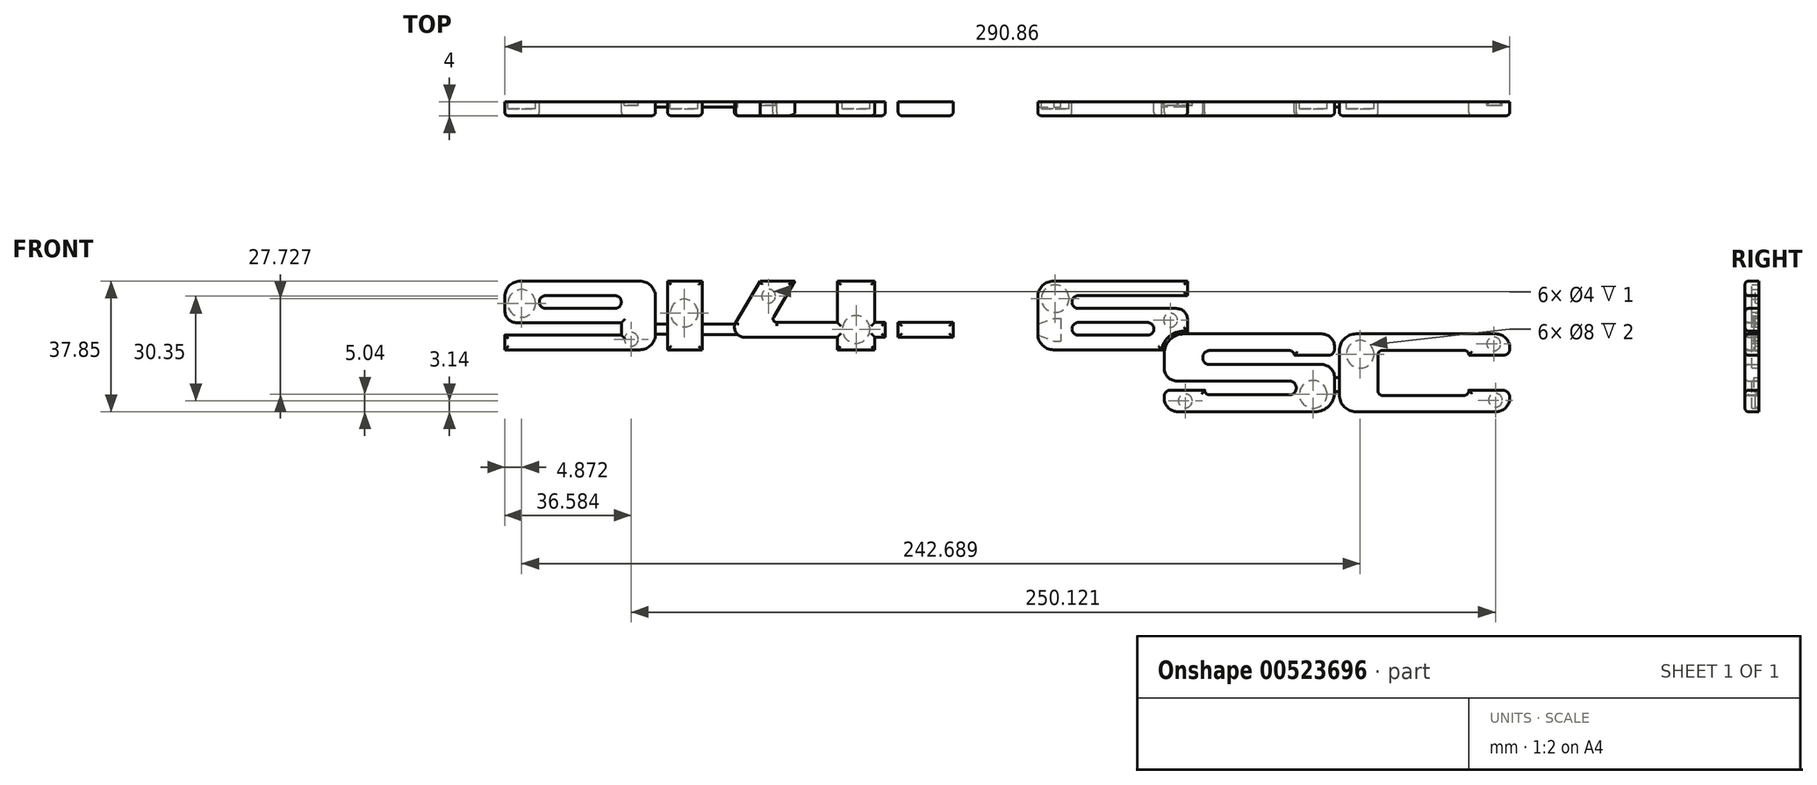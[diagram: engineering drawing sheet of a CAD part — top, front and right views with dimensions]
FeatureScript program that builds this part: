
annotation { "Feature Type Name" : "Feature", "Feature Type Description" : "" }
export const myFeature = defineFeature(function(context is Context, id is Id, definition is map)
    precondition{}
    {
        {
            var Q0;
            Q0=qCreatedBy(makeId("Front.planeOp"),FACE);
            var sketch = newSketch(context, id + "F0", { "sketchPlane" : qUnion([Q0])});
            skPoint(sketch, "E0", {"position": v(-109.13, 31.6) * mm});
            skPoint(sketch, "E1", {"position": v(-109.13, 11.72) * mm});
            skPoint(sketch, "E2", {"position": v(-65.54, 11.72) * mm});
            skPoint(sketch, "E3", {"position": v(-65.54, 31.6) * mm});
            skLineSegment(sketch, "E4.bottom", {"start": v(-104.63, 31.6) * mm, "end": v(-70.04, 31.6) * mm});
            skLineSegment(sketch, "E4.top", {"start": v(-109.13, 11.72) * mm, "end": v(-70.04, 11.72) * mm});
            skLineSegment(sketch, "E4.left", {"start": v(-109.13, 27.1) * mm, "end": v(-109.13, 23.04) * mm});
            skLineSegment(sketch, "E4.right", {"start": v(-65.54, 27.1) * mm, "end": v(-65.54, 16.22) * mm});
            skLineSegment(sketch, "E5.bottom", {"start": v(-109.13, 15.99) * mm, "end": v(-75.41, 15.99) * mm});
            skLineSegment(sketch, "E5.top", {"start": v(-105.62, 19.53) * mm, "end": v(-75.41, 19.53) * mm});
            skLineSegment(sketch, "E5.right", {"start": v(-75.41, 15.99) * mm, "end": v(-75.41, 19.53) * mm});
            skLineSegment(sketch, "E6.bottom", {"start": v(-77.15, 23.72) * mm, "end": v(-97.43, 23.72) * mm});
            skLineSegment(sketch, "E6.top", {"start": v(-77.15, 27.36) * mm, "end": v(-97.43, 27.36) * mm});
            skLineSegment(sketch, "E6.left", {"start": v(-75.41, 25.46) * mm, "end": v(-75.41, 25.62) * mm});
            skLineSegment(sketch, "E6.right", {"start": v(-99.16, 25.46) * mm, "end": v(-99.16, 25.62) * mm});
            skArc(sketch, "E7.filletArc", {"start": v(-104.63, 31.6) * mm, "mid": v(-107.81, 30.29) * mm, "end": v(-109.13, 27.1) * mm});
            skArc(sketch, "E8.filletArc", {"start": v(-65.54, 27.1) * mm, "mid": v(-66.86, 30.29) * mm, "end": v(-70.04, 31.6) * mm});
            skArc(sketch, "E9.filletArc", {"start": v(-70.04, 11.72) * mm, "mid": v(-66.86, 13.04) * mm, "end": v(-65.54, 16.22) * mm});
            skPoint(sketch, "E10.visualSharp", {"position": v(-99.16, 27.36) * mm});
            skArc(sketch, "E10.filletArc", {"start": v(-97.43, 27.36) * mm, "mid": v(-98.65, 26.85) * mm, "end": v(-99.16, 25.62) * mm});
            skPoint(sketch, "E11.visualSharp", {"position": v(-99.16, 23.72) * mm});
            skArc(sketch, "E11.filletArc", {"start": v(-99.16, 25.46) * mm, "mid": v(-98.65, 24.23) * mm, "end": v(-97.43, 23.72) * mm});
            skPoint(sketch, "E12.visualSharp", {"position": v(-75.41, 27.36) * mm});
            skArc(sketch, "E12.filletArc", {"start": v(-75.41, 25.62) * mm, "mid": v(-75.92, 26.85) * mm, "end": v(-77.15, 27.36) * mm});
            skPoint(sketch, "E13.visualSharp", {"position": v(-75.41, 23.72) * mm});
            skArc(sketch, "E13.filletArc", {"start": v(-77.15, 23.72) * mm, "mid": v(-75.92, 24.23) * mm, "end": v(-75.41, 25.46) * mm});
            skLineSegment(sketch, "E14.trimOffspring", {"start": v(-109.13, 15.99) * mm, "end": v(-109.13, 11.72) * mm});
            skPoint(sketch, "E15.visualSharp", {"position": v(-109.13, 19.53) * mm});
            skArc(sketch, "E15.filletArc", {"start": v(-109.13, 23.04) * mm, "mid": v(-108.1, 20.56) * mm, "end": v(-105.62, 19.53) * mm});
            skLineSegment(sketch, "E16", {"start": v(-62.04, 31.6) * mm, "end": v(-52.01, 31.6) * mm});
            skLineSegment(sketch, "E17", {"start": v(-62.04, 11.72) * mm, "end": v(-52.01, 11.72) * mm});
            skLineSegment(sketch, "E18.left", {"start": v(-62.04, 31.6) * mm, "end": v(-62.04, 11.72) * mm});
            skLineSegment(sketch, "E18.right", {"start": v(-52.01, 31.6) * mm, "end": v(-52.01, 11.72) * mm});
            skLineSegment(sketch, "E19", {"start": v(-31.25, 31.6) * mm, "end": v(-25.18, 31.6) * mm});
            skLineSegment(sketch, "E20.bottom", {"start": v(-12.94, 31.6) * mm, "end": v(-2.03, 31.6) * mm});
            skLineSegment(sketch, "E20.top", {"start": v(-12.94, 11.72) * mm, "end": v(-2.03, 11.72) * mm});
            skLineSegment(sketch, "E20.left", {"start": v(-12.94, 31.6) * mm, "end": v(-12.94, 19.68) * mm});
            skLineSegment(sketch, "E20.right", {"start": v(-2.03, 31.6) * mm, "end": v(-2.03, 19.68) * mm});
            skLineSegment(sketch, "E21.bottom", {"start": v(0.96, 19.68) * mm, "end": v(-2.03, 19.68) * mm});
            skLineSegment(sketch, "E21.top", {"start": v(0.96, 15.35) * mm, "end": v(-2.03, 15.35) * mm});
            skLineSegment(sketch, "E21.left", {"start": v(0.96, 19.68) * mm, "end": v(0.96, 15.35) * mm});
            skLineSegment(sketch, "E22", {"start": v(-35.26, 31.6) * mm, "end": v(-42.35, 19.59) * mm});
            skLineSegment(sketch, "E23", {"start": v(-25.18, 31.6) * mm, "end": v(-31.35, 21.25) * mm});
            skPoint(sketch, "E24", {"position": v(-30.43, 19.68) * mm});
            skLineSegment(sketch, "E25.trimOffspring", {"start": v(-12.94, 15.35) * mm, "end": v(-12.94, 11.72) * mm});
            skLineSegment(sketch, "E26.trimOffspring", {"start": v(-12.94, 15.35) * mm, "end": v(-39.77, 15.35) * mm});
            skLineSegment(sketch, "E27.trimOffspring", {"start": v(-2.03, 15.35) * mm, "end": v(-2.03, 11.72) * mm});
            skLineSegment(sketch, "E28.trimOffspring", {"start": v(-12.94, 19.68) * mm, "end": v(-30.43, 19.68) * mm});
            skLineSegment(sketch, "E29.trimOffspring", {"start": v(-35.26, 31.6) * mm, "end": v(-31.25, 31.6) * mm});
            skArc(sketch, "E30", {"start": v(-42.35, 19.59) * mm, "mid": v(-42.25, 16.75) * mm, "end": v(-39.77, 15.35) * mm});
            skArc(sketch, "E31", {"start": v(-31.35, 21.25) * mm, "mid": v(-31.35, 20.2) * mm, "end": v(-30.43, 19.68) * mm});
            skLineSegment(sketch, "E32", {"start": v(49.66, 31.6) * mm, "end": v(88.48, 31.6) * mm});
            skLineSegment(sketch, "E33", {"start": v(49.66, 11.72) * mm, "end": v(80.81, 11.72) * mm});
            skLineSegment(sketch, "E34.bottom", {"start": v(4.7, 19.69) * mm, "end": v(20.61, 19.69) * mm});
            skLineSegment(sketch, "E34.top", {"start": v(4.7, 15.35) * mm, "end": v(20.61, 15.35) * mm});
            skLineSegment(sketch, "E34.left", {"start": v(4.7, 19.69) * mm, "end": v(4.7, 15.35) * mm});
            skLineSegment(sketch, "E34.right", {"start": v(20.61, 19.69) * mm, "end": v(20.61, 15.35) * mm});
            skLineSegment(sketch, "E35", {"start": v(45.1, 26.4) * mm, "end": v(45.1, 16.28) * mm});
            skLineSegment(sketch, "E36", {"start": v(45.1, 26.4) * mm, "end": v(45.1, 27.06) * mm});
            skLineSegment(sketch, "E37", {"start": v(88.48, 31.6) * mm, "end": v(88.48, 27.39) * mm});
            skLineSegment(sketch, "E38.bottom", {"start": v(88.48, 27.39) * mm, "end": v(56.83, 27.39) * mm});
            skLineSegment(sketch, "E38.top", {"start": v(85.22, 23.67) * mm, "end": v(56.83, 23.67) * mm});
            skLineSegment(sketch, "E38.right", {"start": v(55, 25.56) * mm, "end": v(55, 25.5) * mm});
            skLineSegment(sketch, "E39.bottom", {"start": v(56.83, 19.61) * mm, "end": v(76.9, 19.61) * mm});
            skLineSegment(sketch, "E39.top", {"start": v(56.83, 15.93) * mm, "end": v(76.9, 15.93) * mm});
            skLineSegment(sketch, "E39.left", {"start": v(55, 17.78) * mm, "end": v(55, 17.76) * mm});
            skLineSegment(sketch, "E39.right", {"start": v(78.72, 17.78) * mm, "end": v(78.72, 17.76) * mm});
            skLineSegment(sketch, "E40.trimOffspring", {"start": v(88.48, 20.42) * mm, "end": v(88.48, 17.15) * mm});
            skPoint(sketch, "E41.visualSharp", {"position": v(45.1, 31.6) * mm});
            skArc(sketch, "E41.filletArc", {"start": v(49.66, 31.6) * mm, "mid": v(46.44, 30.27) * mm, "end": v(45.1, 27.06) * mm});
            skPoint(sketch, "E42.visualSharp", {"position": v(45.1, 11.72) * mm});
            skArc(sketch, "E42.filletArc", {"start": v(45.1, 16.28) * mm, "mid": v(46.44, 13.06) * mm, "end": v(49.66, 11.72) * mm});
            skPoint(sketch, "E43.visualSharp", {"position": v(88.48, 23.67) * mm});
            skArc(sketch, "E43.filletArc", {"start": v(88.48, 20.42) * mm, "mid": v(87.52, 22.72) * mm, "end": v(85.22, 23.67) * mm});
            skPoint(sketch, "E44.visualSharp", {"position": v(55, 27.39) * mm});
            skArc(sketch, "E44.filletArc", {"start": v(56.83, 27.39) * mm, "mid": v(55.54, 26.85) * mm, "end": v(55, 25.56) * mm});
            skPoint(sketch, "E45.visualSharp", {"position": v(55, 23.67) * mm});
            skArc(sketch, "E45.filletArc", {"start": v(55, 25.5) * mm, "mid": v(55.54, 24.21) * mm, "end": v(56.83, 23.67) * mm});
            skPoint(sketch, "E46.visualSharp", {"position": v(55, 19.61) * mm});
            skArc(sketch, "E46.filletArc", {"start": v(56.83, 19.61) * mm, "mid": v(55.54, 19.08) * mm, "end": v(55, 17.78) * mm});
            skPoint(sketch, "E47.visualSharp", {"position": v(55, 15.93) * mm});
            skArc(sketch, "E47.filletArc", {"start": v(55, 17.76) * mm, "mid": v(55.54, 16.47) * mm, "end": v(56.83, 15.93) * mm});
            skPoint(sketch, "E48.visualSharp", {"position": v(78.72, 19.61) * mm});
            skArc(sketch, "E48.filletArc", {"start": v(78.72, 17.78) * mm, "mid": v(78.19, 19.08) * mm, "end": v(76.9, 19.61) * mm});
            skPoint(sketch, "E49.visualSharp", {"position": v(78.72, 15.93) * mm});
            skArc(sketch, "E49.filletArc", {"start": v(76.9, 15.93) * mm, "mid": v(78.19, 16.47) * mm, "end": v(78.72, 17.76) * mm});
            skLineSegment(sketch, "E50", {"start": v(81.7, -1.92) * mm, "end": v(81.7, -1.8) * mm});
            skPoint(sketch, "E50.endSnap0", {"position": v(78.19, 16.47) * mm});
            skLineSegment(sketch, "E51", {"start": v(81.7, -1.92) * mm, "end": v(81.7, -2.2) * mm});
            skLineSegment(sketch, "E52", {"start": v(88.1, -6.24) * mm, "end": v(85.74, -6.24) * mm});
            skLineSegment(sketch, "E53", {"start": v(88.1, -6.24) * mm, "end": v(125.36, -6.24) * mm});
            skLineSegment(sketch, "E54", {"start": v(99.4, 16.3) * mm, "end": v(87.35, 16.3) * mm});
            skLineSegment(sketch, "E55", {"start": v(99.4, 16.3) * mm, "end": v(127.31, 16.3) * mm});
            skLineSegment(sketch, "E56", {"start": v(131.01, 2.56) * mm, "end": v(131.01, -0.58) * mm});
            skLineSegment(sketch, "E57", {"start": v(131.01, 2.56) * mm, "end": v(131.01, 3.72) * mm});
            skLineSegment(sketch, "E58", {"start": v(83.49, 0) * mm, "end": v(93.47, 0) * mm});
            skLineSegment(sketch, "E59", {"start": v(103.74, -1.35) * mm, "end": v(94.8, -1.35) * mm});
            skLineSegment(sketch, "E60", {"start": v(103.74, -1.35) * mm, "end": v(117.95, -1.35) * mm});
            skLineSegment(sketch, "E61", {"start": v(102.57, 2.69) * mm, "end": v(85.4, 2.69) * mm});
            skLineSegment(sketch, "E62", {"start": v(102.57, 2.69) * mm, "end": v(117.95, 2.69) * mm});
            skLineSegment(sketch, "E63", {"start": v(107.56, 7.43) * mm, "end": v(94.87, 7.43) * mm});
            skLineSegment(sketch, "E64", {"start": v(107.56, 7.43) * mm, "end": v(127.31, 7.43) * mm});
            skLineSegment(sketch, "E65", {"start": v(103.88, 11.49) * mm, "end": v(94.87, 11.49) * mm});
            skLineSegment(sketch, "E66", {"start": v(103.88, 11.49) * mm, "end": v(118, 11.49) * mm});
            skLineSegment(sketch, "E67", {"start": v(127.71, 10.1) * mm, "end": v(119.36, 10.1) * mm});
            skLineSegment(sketch, "E68", {"start": v(127.71, 10.1) * mm, "end": v(129.16, 10.1) * mm});
            skLineSegment(sketch, "E69", {"start": v(119.36, 10.1) * mm, "end": v(119.36, 10.12) * mm});
            skLineSegment(sketch, "E70.trimOffspring", {"start": v(131.01, 11.96) * mm, "end": v(131.01, 12.6) * mm});
            skLineSegment(sketch, "E71.trimOffspring", {"start": v(81.7, 6.39) * mm, "end": v(81.7, 10.64) * mm});
            skPoint(sketch, "E72.orphan", {"position": v(79.2, 0) * mm});
            skPoint(sketch, "E73.orphan", {"position": v(81.7, -7.6) * mm});
            skLineSegment(sketch, "E74", {"start": v(93.47, 0) * mm, "end": v(93.47, -0.02) * mm});
            skPoint(sketch, "E75.visualSharp", {"position": v(81.7, 16.3) * mm});
            skArc(sketch, "E75.filletArc", {"start": v(87.35, 16.3) * mm, "mid": v(83.35, 14.65) * mm, "end": v(81.7, 10.64) * mm});
            skPoint(sketch, "E76.visualSharp", {"position": v(131.01, -6.24) * mm});
            skArc(sketch, "E76.filletArc", {"start": v(125.36, -6.24) * mm, "mid": v(129.36, -4.58) * mm, "end": v(131.01, -0.58) * mm});
            skPoint(sketch, "E77.visualSharp", {"position": v(81.7, -6.24) * mm});
            skArc(sketch, "E77.filletArc", {"start": v(81.7, -2.2) * mm, "mid": v(82.88, -5.06) * mm, "end": v(85.74, -6.24) * mm});
            skPoint(sketch, "E78.visualSharp", {"position": v(131.01, 16.3) * mm});
            skArc(sketch, "E78.filletArc", {"start": v(131.01, 12.6) * mm, "mid": v(129.93, 15.22) * mm, "end": v(127.31, 16.3) * mm});
            skPoint(sketch, "E79.visualSharp", {"position": v(131.01, 7.43) * mm});
            skArc(sketch, "E79.filletArc", {"start": v(131.01, 3.72) * mm, "mid": v(129.93, 6.34) * mm, "end": v(127.31, 7.43) * mm});
            skPoint(sketch, "E80.visualSharp", {"position": v(81.7, 2.69) * mm});
            skArc(sketch, "E80.filletArc", {"start": v(81.7, 6.39) * mm, "mid": v(82.78, 3.77) * mm, "end": v(85.4, 2.69) * mm});
            skPoint(sketch, "E81.visualSharp", {"position": v(81.7, 0) * mm});
            skArc(sketch, "E81.filletArc", {"start": v(83.49, 0) * mm, "mid": v(82.22, -0.53) * mm, "end": v(81.7, -1.8) * mm});
            skPoint(sketch, "E82.visualSharp", {"position": v(131.01, 10.1) * mm});
            skArc(sketch, "E82.filletArc", {"start": v(129.16, 10.1) * mm, "mid": v(130.47, 10.65) * mm, "end": v(131.01, 11.96) * mm});
            skLineSegment(sketch, "E83", {"start": v(92.9, 9.5) * mm, "end": v(92.9, 9.4) * mm});
            skPoint(sketch, "E84.visualSharp", {"position": v(92.9, 11.49) * mm});
            skArc(sketch, "E84.filletArc", {"start": v(94.87, 11.49) * mm, "mid": v(93.47, 10.9) * mm, "end": v(92.9, 9.5) * mm});
            skPoint(sketch, "E85.visualSharp", {"position": v(92.9, 7.43) * mm});
            skArc(sketch, "E85.filletArc", {"start": v(92.9, 9.4) * mm, "mid": v(93.47, 8) * mm, "end": v(94.87, 7.43) * mm});
            skLineSegment(sketch, "E86", {"start": v(119.93, 0.7) * mm, "end": v(119.93, 0.63) * mm});
            skPoint(sketch, "E87.visualSharp", {"position": v(119.93, 2.69) * mm});
            skArc(sketch, "E87.filletArc", {"start": v(119.93, 0.7) * mm, "mid": v(119.35, 2.1) * mm, "end": v(117.95, 2.69) * mm});
            skPoint(sketch, "E88.visualSharp", {"position": v(119.93, -1.35) * mm});
            skArc(sketch, "E88.filletArc", {"start": v(117.95, -1.35) * mm, "mid": v(119.35, -0.77) * mm, "end": v(119.93, 0.63) * mm});
            skPoint(sketch, "E89.visualSharp", {"position": v(93.47, -1.35) * mm});
            skArc(sketch, "E89.filletArc", {"start": v(93.47, -0.02) * mm, "mid": v(93.85, -0.96) * mm, "end": v(94.8, -1.35) * mm});
            skPoint(sketch, "E90.visualSharp", {"position": v(119.36, 11.49) * mm});
            skArc(sketch, "E90.filletArc", {"start": v(119.36, 10.12) * mm, "mid": v(118.96, 11.09) * mm, "end": v(118, 11.49) * mm});
            skPoint(sketch, "E91", {"position": v(132.39, 16.3) * mm});
            skPoint(sketch, "E92", {"position": v(132.39, -6.24) * mm});
            skPoint(sketch, "E93", {"position": v(181.73, -6.24) * mm});
            skPoint(sketch, "E94", {"position": v(181.73, 16.3) * mm});
            skLineSegment(sketch, "E95.bottom", {"start": v(137.28, 16.3) * mm, "end": v(177.7, 16.3) * mm});
            skLineSegment(sketch, "E95.top", {"start": v(137.28, -6.24) * mm, "end": v(177.7, -6.24) * mm});
            skLineSegment(sketch, "E95.left", {"start": v(132.39, 11.41) * mm, "end": v(132.39, -1.35) * mm});
            skLineSegment(sketch, "E95.right", {"start": v(181.73, 12.27) * mm, "end": v(181.73, 11.93) * mm});
            skLineSegment(sketch, "E96", {"start": v(143.6, 5.48) * mm, "end": v(143.6, 10.24) * mm});
            skLineSegment(sketch, "E97", {"start": v(179.7, 0) * mm, "end": v(169.84, 0) * mm});
            skLineSegment(sketch, "E98", {"start": v(178.06, 10.13) * mm, "end": v(169.84, 10.13) * mm});
            skLineSegment(sketch, "E99", {"start": v(178.06, 10.13) * mm, "end": v(179.93, 10.13) * mm});
            skLineSegment(sketch, "E100", {"start": v(160.57, 11.56) * mm, "end": v(144.9, 11.56) * mm});
            skLineSegment(sketch, "E101", {"start": v(160.57, 11.56) * mm, "end": v(168.53, 11.56) * mm});
            skLineSegment(sketch, "E102", {"start": v(169.84, 10.13) * mm, "end": v(169.84, 10.24) * mm});
            skLineSegment(sketch, "E103.trimOffspring", {"start": v(181.73, -2.03) * mm, "end": v(181.73, -2.21) * mm});
            skArc(sketch, "E104.filletArc", {"start": v(137.28, 16.3) * mm, "mid": v(133.82, 14.87) * mm, "end": v(132.39, 11.41) * mm});
            skArc(sketch, "E105.filletArc", {"start": v(132.39, -1.35) * mm, "mid": v(133.82, -4.8) * mm, "end": v(137.28, -6.24) * mm});
            skArc(sketch, "E106.filletArc", {"start": v(181.73, 12.27) * mm, "mid": v(180.55, 15.12) * mm, "end": v(177.7, 16.3) * mm});
            skArc(sketch, "E107.filletArc", {"start": v(177.7, -6.24) * mm, "mid": v(180.55, -5.06) * mm, "end": v(181.73, -2.21) * mm});
            skPoint(sketch, "E108.visualSharp", {"position": v(181.73, 10.13) * mm});
            skArc(sketch, "E108.filletArc", {"start": v(179.93, 10.13) * mm, "mid": v(181.2, 10.66) * mm, "end": v(181.73, 11.93) * mm});
            skPoint(sketch, "E109.visualSharp", {"position": v(181.73, 0) * mm});
            skArc(sketch, "E109.filletArc", {"start": v(181.73, -2.03) * mm, "mid": v(181.13, -0.6) * mm, "end": v(179.7, 0) * mm});
            skLineSegment(sketch, "E110", {"start": v(143.6, 5.48) * mm, "end": v(143.6, -0.2) * mm});
            skLineSegment(sketch, "E111", {"start": v(150.45, -1.52) * mm, "end": v(144.9, -1.52) * mm});
            skLineSegment(sketch, "E112", {"start": v(150.45, -1.52) * mm, "end": v(168.53, -1.52) * mm});
            skLineSegment(sketch, "E113", {"start": v(169.84, 0) * mm, "end": v(169.84, -0.2) * mm});
            skPoint(sketch, "E114.visualSharp", {"position": v(169.84, 11.56) * mm});
            skArc(sketch, "E114.filletArc", {"start": v(169.84, 10.24) * mm, "mid": v(169.46, 11.17) * mm, "end": v(168.53, 11.56) * mm});
            skPoint(sketch, "E115.visualSharp", {"position": v(169.84, -1.52) * mm});
            skArc(sketch, "E115.filletArc", {"start": v(168.53, -1.52) * mm, "mid": v(169.46, -1.14) * mm, "end": v(169.84, -0.2) * mm});
            skPoint(sketch, "E116.visualSharp", {"position": v(143.6, 11.56) * mm});
            skArc(sketch, "E116.filletArc", {"start": v(144.9, 11.56) * mm, "mid": v(143.98, 11.17) * mm, "end": v(143.6, 10.24) * mm});
            skPoint(sketch, "E117.visualSharp", {"position": v(143.6, -1.52) * mm});
            skArc(sketch, "E117.filletArc", {"start": v(143.6, -0.2) * mm, "mid": v(143.98, -1.14) * mm, "end": v(144.9, -1.52) * mm});
            skLineSegment(sketch, "E118", {"start": v(-0.53, 19.68) * mm, "end": v(0.96, 19.68) * mm});
            skLineSegment(sketch, "E119", {"start": v(-0.33, 15.35) * mm, "end": v(0.96, 15.35) * mm});
            skPoint(sketch, "E120", {"position": v(88.48, 16.3) * mm});
            skPoint(sketch, "E121", {"position": v(81.8, 11.72) * mm});
            skArc(sketch, "E122.0", {"start": v(87.35, 17.15) * mm, "mid": v(83.15, 15.61) * mm, "end": v(80.94, 11.72) * mm});
            skLineSegment(sketch, "E122.1", {"start": v(88.48, 17.15) * mm, "end": v(87.35, 17.15) * mm});
            skLineSegment(sketch, "E123", {"start": v(80.55, 11.72) * mm, "end": v(80.94, 11.72) * mm});
            skPoint(sketch, "E124", {"position": v(45.1, 19.1) * mm});
            skLineSegment(sketch, "E125", {"start": v(45.1, 19.1) * mm, "end": v(49.87, 20.81) * mm});
            skLineSegment(sketch, "E126", {"start": v(45.12, 15.95) * mm, "end": v(49.87, 14.23) * mm});
            skLineSegment(sketch, "E127", {"start": v(51.8, 20.81) * mm, "end": v(51.8, 14.23) * mm});
            skLineSegment(sketch, "E128", {"start": v(49.87, 20.81) * mm, "end": v(51.8, 20.81) * mm});
            skLineSegment(sketch, "E129", {"start": v(49.87, 14.23) * mm, "end": v(51.8, 14.23) * mm});
            skSolve(sketch);
        }
        {
            var Q0;
            Q0=qCreatedBy(makeId("Front.planeOp"),FACE);
            var sketch = newSketch(context, id + "F1", { "sketchPlane" : qUnion([Q0])});
            skPoint(sketch, "E130.0", {"position": v(-109.13, 31.6) * mm});
            skPoint(sketch, "E130.1", {"position": v(-109.13, 11.72) * mm});
            skPoint(sketch, "E130.2", {"position": v(-65.54, 11.72) * mm});
            skPoint(sketch, "E130.3", {"position": v(-65.54, 31.6) * mm});
            skLineSegment(sketch, "E130.4", {"start": v(-104.63, 31.6) * mm, "end": v(-70.04, 31.6) * mm});
            skLineSegment(sketch, "E130.5", {"start": v(-109.13, 11.72) * mm, "end": v(-70.04, 11.72) * mm});
            skLineSegment(sketch, "E130.6", {"start": v(-109.13, 27.1) * mm, "end": v(-109.13, 23.04) * mm});
            skLineSegment(sketch, "E130.7", {"start": v(-65.54, 27.1) * mm, "end": v(-65.54, 16.22) * mm});
            skLineSegment(sketch, "E130.8", {"start": v(-109.13, 15.99) * mm, "end": v(-75.41, 15.99) * mm});
            skLineSegment(sketch, "E130.9", {"start": v(-105.62, 19.53) * mm, "end": v(-75.41, 19.53) * mm});
            skLineSegment(sketch, "E130.10", {"start": v(-75.41, 15.99) * mm, "end": v(-75.41, 19.53) * mm});
            skLineSegment(sketch, "E130.11", {"start": v(-77.15, 23.72) * mm, "end": v(-97.43, 23.72) * mm});
            skLineSegment(sketch, "E130.12", {"start": v(-77.15, 27.36) * mm, "end": v(-97.43, 27.36) * mm});
            skLineSegment(sketch, "E130.13", {"start": v(-75.41, 25.46) * mm, "end": v(-75.41, 25.62) * mm});
            skLineSegment(sketch, "E130.14", {"start": v(-99.16, 25.46) * mm, "end": v(-99.16, 25.62) * mm});
            skPoint(sketch, "E130.15", {"position": v(-109.13, 31.6) * mm});
            skArc(sketch, "E130.16", {"start": v(-104.63, 31.6) * mm, "mid": v(-107.81, 30.29) * mm, "end": v(-109.13, 27.1) * mm});
            skPoint(sketch, "E130.17", {"position": v(-65.54, 31.6) * mm});
            skArc(sketch, "E130.18", {"start": v(-65.54, 27.1) * mm, "mid": v(-66.86, 30.29) * mm, "end": v(-70.04, 31.6) * mm});
            skPoint(sketch, "E130.19", {"position": v(-65.54, 11.72) * mm});
            skArc(sketch, "E130.20", {"start": v(-70.04, 11.72) * mm, "mid": v(-66.86, 13.04) * mm, "end": v(-65.54, 16.22) * mm});
            skPoint(sketch, "E130.21", {"position": v(-99.16, 27.36) * mm});
            skArc(sketch, "E130.22", {"start": v(-97.43, 27.36) * mm, "mid": v(-98.65, 26.85) * mm, "end": v(-99.16, 25.62) * mm});
            skPoint(sketch, "E130.23", {"position": v(-99.16, 23.72) * mm});
            skArc(sketch, "E130.24", {"start": v(-99.16, 25.46) * mm, "mid": v(-98.65, 24.23) * mm, "end": v(-97.43, 23.72) * mm});
            skPoint(sketch, "E130.25", {"position": v(-75.41, 27.36) * mm});
            skArc(sketch, "E130.26", {"start": v(-75.41, 25.62) * mm, "mid": v(-75.92, 26.85) * mm, "end": v(-77.15, 27.36) * mm});
            skPoint(sketch, "E130.27", {"position": v(-75.41, 23.72) * mm});
            skArc(sketch, "E130.28", {"start": v(-77.15, 23.72) * mm, "mid": v(-75.92, 24.23) * mm, "end": v(-75.41, 25.46) * mm});
            skLineSegment(sketch, "E130.29", {"start": v(-109.13, 15.99) * mm, "end": v(-109.13, 11.72) * mm});
            skPoint(sketch, "E130.30", {"position": v(-109.13, 19.53) * mm});
            skArc(sketch, "E130.31", {"start": v(-109.13, 23.04) * mm, "mid": v(-108.1, 20.56) * mm, "end": v(-105.62, 19.53) * mm});
            skLineSegment(sketch, "E130.32", {"start": v(-62.04, 31.6) * mm, "end": v(-52.01, 31.6) * mm});
            skLineSegment(sketch, "E130.33", {"start": v(-62.04, 11.72) * mm, "end": v(-52.01, 11.72) * mm});
            skLineSegment(sketch, "E130.34", {"start": v(-62.04, 31.6) * mm, "end": v(-52.01, 31.6) * mm});
            skLineSegment(sketch, "E130.35", {"start": v(-62.04, 11.72) * mm, "end": v(-52.01, 11.72) * mm});
            skLineSegment(sketch, "E130.36", {"start": v(-62.04, 31.6) * mm, "end": v(-62.04, 11.72) * mm});
            skLineSegment(sketch, "E130.37", {"start": v(-52.01, 31.6) * mm, "end": v(-52.01, 11.72) * mm});
            skLineSegment(sketch, "E130.38", {"start": v(-31.25, 31.6) * mm, "end": v(-25.18, 31.6) * mm});
            skLineSegment(sketch, "E130.39", {"start": v(-12.94, 31.6) * mm, "end": v(-2.03, 31.6) * mm});
            skLineSegment(sketch, "E130.40", {"start": v(-12.94, 11.72) * mm, "end": v(-2.03, 11.72) * mm});
            skLineSegment(sketch, "E130.41", {"start": v(-12.94, 31.6) * mm, "end": v(-12.94, 19.68) * mm});
            skLineSegment(sketch, "E130.42", {"start": v(-2.03, 31.6) * mm, "end": v(-2.03, 19.68) * mm});
            skLineSegment(sketch, "E130.43", {"start": v(0.96, 19.68) * mm, "end": v(-2.03, 19.68) * mm});
            skLineSegment(sketch, "E130.44", {"start": v(0.96, 15.35) * mm, "end": v(-2.03, 15.35) * mm});
            skLineSegment(sketch, "E130.45", {"start": v(0.96, 19.68) * mm, "end": v(0.96, 15.35) * mm});
            skLineSegment(sketch, "E130.46", {"start": v(-35.26, 31.6) * mm, "end": v(-42.35, 19.59) * mm});
            skLineSegment(sketch, "E130.47", {"start": v(-25.18, 31.6) * mm, "end": v(-31.35, 21.25) * mm});
            skPoint(sketch, "E130.48", {"position": v(-30.43, 19.68) * mm});
            skLineSegment(sketch, "E130.49", {"start": v(-12.94, 15.35) * mm, "end": v(-12.94, 11.72) * mm});
            skLineSegment(sketch, "E130.50", {"start": v(-12.94, 15.35) * mm, "end": v(-39.77, 15.35) * mm});
            skLineSegment(sketch, "E130.51", {"start": v(-2.03, 15.35) * mm, "end": v(-2.03, 11.72) * mm});
            skLineSegment(sketch, "E130.52", {"start": v(-12.94, 19.68) * mm, "end": v(-30.43, 19.68) * mm});
            skLineSegment(sketch, "E130.53", {"start": v(-12.94, 11.72) * mm, "end": v(-2.03, 11.72) * mm});
            skLineSegment(sketch, "E130.54", {"start": v(-12.94, 31.6) * mm, "end": v(-2.03, 31.6) * mm});
            skLineSegment(sketch, "E130.55", {"start": v(-35.26, 31.6) * mm, "end": v(-31.25, 31.6) * mm});
            skArc(sketch, "E130.56", {"start": v(-42.35, 19.59) * mm, "mid": v(-42.25, 16.75) * mm, "end": v(-39.77, 15.35) * mm});
            skArc(sketch, "E130.57", {"start": v(-31.35, 21.25) * mm, "mid": v(-31.35, 20.2) * mm, "end": v(-30.43, 19.68) * mm});
            skLineSegment(sketch, "E130.58", {"start": v(49.66, 31.6) * mm, "end": v(88.48, 31.6) * mm});
            skLineSegment(sketch, "E130.59", {"start": v(49.66, 11.72) * mm, "end": v(80.81, 11.72) * mm});
            skLineSegment(sketch, "E130.60", {"start": v(4.7, 19.69) * mm, "end": v(20.61, 19.69) * mm});
            skLineSegment(sketch, "E130.61", {"start": v(4.7, 15.35) * mm, "end": v(20.61, 15.35) * mm});
            skLineSegment(sketch, "E130.62", {"start": v(4.7, 19.69) * mm, "end": v(4.7, 15.35) * mm});
            skLineSegment(sketch, "E130.63", {"start": v(20.61, 19.69) * mm, "end": v(20.61, 15.35) * mm});
            skLineSegment(sketch, "E130.64", {"start": v(45.1, 26.4) * mm, "end": v(45.1, 16.28) * mm});
            skLineSegment(sketch, "E130.65", {"start": v(45.1, 26.4) * mm, "end": v(45.1, 27.06) * mm});
            skLineSegment(sketch, "E130.66", {"start": v(88.48, 31.6) * mm, "end": v(88.48, 27.39) * mm});
            skLineSegment(sketch, "E130.67", {"start": v(88.48, 27.39) * mm, "end": v(56.83, 27.39) * mm});
            skLineSegment(sketch, "E130.68", {"start": v(85.22, 23.67) * mm, "end": v(56.83, 23.67) * mm});
            skLineSegment(sketch, "E130.69", {"start": v(55, 25.56) * mm, "end": v(55, 25.5) * mm});
            skLineSegment(sketch, "E130.70", {"start": v(56.83, 19.61) * mm, "end": v(76.9, 19.61) * mm});
            skLineSegment(sketch, "E130.71", {"start": v(56.83, 15.93) * mm, "end": v(76.9, 15.93) * mm});
            skLineSegment(sketch, "E130.72", {"start": v(55, 17.78) * mm, "end": v(55, 17.76) * mm});
            skLineSegment(sketch, "E130.73", {"start": v(78.72, 17.78) * mm, "end": v(78.72, 17.76) * mm});
            skLineSegment(sketch, "E130.74", {"start": v(88.48, 20.42) * mm, "end": v(88.48, 17.15) * mm});
            skPoint(sketch, "E130.77", {"position": v(45.1, 31.6) * mm});
            skArc(sketch, "E130.78", {"start": v(49.66, 31.6) * mm, "mid": v(46.44, 30.27) * mm, "end": v(45.1, 27.06) * mm});
            skPoint(sketch, "E130.79", {"position": v(45.1, 11.72) * mm});
            skArc(sketch, "E130.80", {"start": v(45.1, 16.28) * mm, "mid": v(46.44, 13.06) * mm, "end": v(49.66, 11.72) * mm});
            skPoint(sketch, "E130.81", {"position": v(88.48, 23.67) * mm});
            skArc(sketch, "E130.82", {"start": v(88.48, 20.42) * mm, "mid": v(87.52, 22.72) * mm, "end": v(85.22, 23.67) * mm});
            skPoint(sketch, "E130.83", {"position": v(55, 27.39) * mm});
            skArc(sketch, "E130.84", {"start": v(56.83, 27.39) * mm, "mid": v(55.54, 26.85) * mm, "end": v(55, 25.56) * mm});
            skPoint(sketch, "E130.85", {"position": v(55, 23.67) * mm});
            skArc(sketch, "E130.86", {"start": v(55, 25.5) * mm, "mid": v(55.54, 24.21) * mm, "end": v(56.83, 23.67) * mm});
            skPoint(sketch, "E130.87", {"position": v(55, 19.61) * mm});
            skArc(sketch, "E130.88", {"start": v(56.83, 19.61) * mm, "mid": v(55.54, 19.08) * mm, "end": v(55, 17.78) * mm});
            skPoint(sketch, "E130.89", {"position": v(55, 15.93) * mm});
            skArc(sketch, "E130.90", {"start": v(55, 17.76) * mm, "mid": v(55.54, 16.47) * mm, "end": v(56.83, 15.93) * mm});
            skPoint(sketch, "E130.91", {"position": v(78.72, 19.61) * mm});
            skArc(sketch, "E130.92", {"start": v(78.72, 17.78) * mm, "mid": v(78.19, 19.08) * mm, "end": v(76.9, 19.61) * mm});
            skPoint(sketch, "E130.93", {"position": v(78.72, 15.93) * mm});
            skArc(sketch, "E130.94", {"start": v(76.9, 15.93) * mm, "mid": v(78.19, 16.47) * mm, "end": v(78.72, 17.76) * mm});
            skLineSegment(sketch, "E130.95", {"start": v(81.7, -1.92) * mm, "end": v(81.7, -1.8) * mm});
            skPoint(sketch, "E130.96", {"position": v(78.19, 16.47) * mm});
            skLineSegment(sketch, "E130.97", {"start": v(81.7, -1.92) * mm, "end": v(81.7, -2.2) * mm});
            skLineSegment(sketch, "E130.98", {"start": v(88.1, -6.24) * mm, "end": v(85.74, -6.24) * mm});
            skLineSegment(sketch, "E130.99", {"start": v(88.1, -6.24) * mm, "end": v(125.36, -6.24) * mm});
            skLineSegment(sketch, "E130.100", {"start": v(99.4, 16.3) * mm, "end": v(87.35, 16.3) * mm});
            skLineSegment(sketch, "E130.101", {"start": v(99.4, 16.3) * mm, "end": v(127.31, 16.3) * mm});
            skLineSegment(sketch, "E130.102", {"start": v(131.01, 2.56) * mm, "end": v(131.01, -0.58) * mm});
            skLineSegment(sketch, "E130.103", {"start": v(131.01, 2.56) * mm, "end": v(131.01, 3.72) * mm});
            skLineSegment(sketch, "E130.104", {"start": v(83.49, 0) * mm, "end": v(93.47, 0) * mm});
            skLineSegment(sketch, "E130.105", {"start": v(103.74, -1.35) * mm, "end": v(94.8, -1.35) * mm});
            skLineSegment(sketch, "E130.106", {"start": v(103.74, -1.35) * mm, "end": v(117.95, -1.35) * mm});
            skLineSegment(sketch, "E130.107", {"start": v(102.57, 2.69) * mm, "end": v(85.4, 2.69) * mm});
            skLineSegment(sketch, "E130.108", {"start": v(102.57, 2.69) * mm, "end": v(117.95, 2.69) * mm});
            skLineSegment(sketch, "E130.109", {"start": v(107.56, 7.43) * mm, "end": v(94.87, 7.43) * mm});
            skLineSegment(sketch, "E130.110", {"start": v(107.56, 7.43) * mm, "end": v(127.31, 7.43) * mm});
            skLineSegment(sketch, "E130.111", {"start": v(103.88, 11.49) * mm, "end": v(94.87, 11.49) * mm});
            skLineSegment(sketch, "E130.112", {"start": v(103.88, 11.49) * mm, "end": v(118, 11.49) * mm});
            skLineSegment(sketch, "E130.113", {"start": v(127.71, 10.1) * mm, "end": v(119.36, 10.1) * mm});
            skLineSegment(sketch, "E130.114", {"start": v(127.71, 10.1) * mm, "end": v(129.16, 10.1) * mm});
            skLineSegment(sketch, "E130.115", {"start": v(119.36, 10.1) * mm, "end": v(119.36, 10.12) * mm});
            skLineSegment(sketch, "E130.116", {"start": v(131.01, 11.96) * mm, "end": v(131.01, 12.6) * mm});
            skLineSegment(sketch, "E130.117", {"start": v(81.7, 6.39) * mm, "end": v(81.7, 10.64) * mm});
            skPoint(sketch, "E130.118", {"position": v(79.2, 0) * mm});
            skPoint(sketch, "E130.119", {"position": v(81.7, -7.6) * mm});
            skLineSegment(sketch, "E130.120", {"start": v(93.47, 0) * mm, "end": v(93.47, -0.02) * mm});
            skPoint(sketch, "E130.121", {"position": v(81.7, 16.3) * mm});
            skArc(sketch, "E130.122", {"start": v(87.35, 16.3) * mm, "mid": v(83.35, 14.65) * mm, "end": v(81.7, 10.64) * mm});
            skPoint(sketch, "E130.123", {"position": v(131.01, -6.24) * mm});
            skArc(sketch, "E130.124", {"start": v(125.36, -6.24) * mm, "mid": v(129.36, -4.58) * mm, "end": v(131.01, -0.58) * mm});
            skPoint(sketch, "E130.125", {"position": v(81.7, -6.24) * mm});
            skArc(sketch, "E130.126", {"start": v(81.7, -2.2) * mm, "mid": v(82.88, -5.06) * mm, "end": v(85.74, -6.24) * mm});
            skPoint(sketch, "E130.127", {"position": v(131.01, 16.3) * mm});
            skArc(sketch, "E130.128", {"start": v(131.01, 12.6) * mm, "mid": v(129.93, 15.22) * mm, "end": v(127.31, 16.3) * mm});
            skPoint(sketch, "E130.129", {"position": v(131.01, 7.43) * mm});
            skArc(sketch, "E130.130", {"start": v(131.01, 3.72) * mm, "mid": v(129.93, 6.34) * mm, "end": v(127.31, 7.43) * mm});
            skPoint(sketch, "E130.131", {"position": v(81.7, 2.69) * mm});
            skArc(sketch, "E130.132", {"start": v(81.7, 6.39) * mm, "mid": v(82.78, 3.77) * mm, "end": v(85.4, 2.69) * mm});
            skPoint(sketch, "E130.133", {"position": v(81.7, 0) * mm});
            skArc(sketch, "E130.134", {"start": v(83.49, 0) * mm, "mid": v(82.22, -0.53) * mm, "end": v(81.7, -1.8) * mm});
            skPoint(sketch, "E130.135", {"position": v(131.01, 10.1) * mm});
            skArc(sketch, "E130.136", {"start": v(129.16, 10.1) * mm, "mid": v(130.47, 10.65) * mm, "end": v(131.01, 11.96) * mm});
            skLineSegment(sketch, "E130.137", {"start": v(92.9, 9.5) * mm, "end": v(92.9, 9.4) * mm});
            skPoint(sketch, "E130.138", {"position": v(92.9, 11.49) * mm});
            skArc(sketch, "E130.139", {"start": v(94.87, 11.49) * mm, "mid": v(93.47, 10.9) * mm, "end": v(92.9, 9.5) * mm});
            skPoint(sketch, "E130.140", {"position": v(92.9, 7.43) * mm});
            skArc(sketch, "E130.141", {"start": v(92.9, 9.4) * mm, "mid": v(93.47, 8) * mm, "end": v(94.87, 7.43) * mm});
            skLineSegment(sketch, "E130.142", {"start": v(119.93, 0.7) * mm, "end": v(119.93, 0.63) * mm});
            skPoint(sketch, "E130.143", {"position": v(119.93, 2.69) * mm});
            skArc(sketch, "E130.144", {"start": v(119.93, 0.7) * mm, "mid": v(119.35, 2.1) * mm, "end": v(117.95, 2.69) * mm});
            skPoint(sketch, "E130.145", {"position": v(119.93, -1.35) * mm});
            skArc(sketch, "E130.146", {"start": v(117.95, -1.35) * mm, "mid": v(119.35, -0.77) * mm, "end": v(119.93, 0.63) * mm});
            skPoint(sketch, "E130.147", {"position": v(93.47, -1.35) * mm});
            skArc(sketch, "E130.148", {"start": v(93.47, -0.02) * mm, "mid": v(93.85, -0.96) * mm, "end": v(94.8, -1.35) * mm});
            skPoint(sketch, "E130.149", {"position": v(119.36, 11.49) * mm});
            skArc(sketch, "E130.150", {"start": v(119.36, 10.12) * mm, "mid": v(118.96, 11.09) * mm, "end": v(118, 11.49) * mm});
            skPoint(sketch, "E130.151", {"position": v(132.39, 16.3) * mm});
            skPoint(sketch, "E130.152", {"position": v(132.39, -6.24) * mm});
            skPoint(sketch, "E130.153", {"position": v(181.73, -6.24) * mm});
            skPoint(sketch, "E130.154", {"position": v(181.73, 16.3) * mm});
            skLineSegment(sketch, "E130.155", {"start": v(137.28, 16.3) * mm, "end": v(177.7, 16.3) * mm});
            skLineSegment(sketch, "E130.156", {"start": v(137.28, -6.24) * mm, "end": v(177.7, -6.24) * mm});
            skLineSegment(sketch, "E130.157", {"start": v(132.39, 11.41) * mm, "end": v(132.39, -1.35) * mm});
            skLineSegment(sketch, "E130.158", {"start": v(181.73, 12.27) * mm, "end": v(181.73, 11.93) * mm});
            skLineSegment(sketch, "E130.159", {"start": v(143.6, 5.48) * mm, "end": v(143.6, 10.24) * mm});
            skLineSegment(sketch, "E130.160", {"start": v(179.7, 0) * mm, "end": v(169.84, 0) * mm});
            skLineSegment(sketch, "E130.161", {"start": v(178.06, 10.13) * mm, "end": v(169.84, 10.13) * mm});
            skLineSegment(sketch, "E130.162", {"start": v(178.06, 10.13) * mm, "end": v(179.93, 10.13) * mm});
            skLineSegment(sketch, "E130.163", {"start": v(160.57, 11.56) * mm, "end": v(144.9, 11.56) * mm});
            skLineSegment(sketch, "E130.164", {"start": v(160.57, 11.56) * mm, "end": v(168.53, 11.56) * mm});
            skLineSegment(sketch, "E130.165", {"start": v(169.84, 10.13) * mm, "end": v(169.84, 10.24) * mm});
            skLineSegment(sketch, "E130.166", {"start": v(181.73, -2.03) * mm, "end": v(181.73, -2.21) * mm});
            skPoint(sketch, "E130.167", {"position": v(132.39, 16.3) * mm});
            skArc(sketch, "E130.168", {"start": v(137.28, 16.3) * mm, "mid": v(133.82, 14.87) * mm, "end": v(132.39, 11.41) * mm});
            skPoint(sketch, "E130.169", {"position": v(132.39, -6.24) * mm});
            skArc(sketch, "E130.170", {"start": v(132.39, -1.35) * mm, "mid": v(133.82, -4.8) * mm, "end": v(137.28, -6.24) * mm});
            skPoint(sketch, "E130.171", {"position": v(181.73, 16.3) * mm});
            skArc(sketch, "E130.172", {"start": v(181.73, 12.27) * mm, "mid": v(180.55, 15.12) * mm, "end": v(177.7, 16.3) * mm});
            skPoint(sketch, "E130.173", {"position": v(181.73, -6.24) * mm});
            skArc(sketch, "E130.174", {"start": v(177.7, -6.24) * mm, "mid": v(180.55, -5.06) * mm, "end": v(181.73, -2.21) * mm});
            skPoint(sketch, "E130.175", {"position": v(181.73, 10.13) * mm});
            skArc(sketch, "E130.176", {"start": v(179.93, 10.13) * mm, "mid": v(181.2, 10.66) * mm, "end": v(181.73, 11.93) * mm});
            skPoint(sketch, "E130.177", {"position": v(181.73, 0) * mm});
            skArc(sketch, "E130.178", {"start": v(181.73, -2.03) * mm, "mid": v(181.13, -0.6) * mm, "end": v(179.7, 0) * mm});
            skLineSegment(sketch, "E130.179", {"start": v(143.6, 5.48) * mm, "end": v(143.6, -0.2) * mm});
            skLineSegment(sketch, "E130.180", {"start": v(150.45, -1.52) * mm, "end": v(144.9, -1.52) * mm});
            skLineSegment(sketch, "E130.181", {"start": v(150.45, -1.52) * mm, "end": v(168.53, -1.52) * mm});
            skLineSegment(sketch, "E130.182", {"start": v(169.84, 0) * mm, "end": v(169.84, -0.2) * mm});
            skPoint(sketch, "E130.183", {"position": v(169.84, 11.56) * mm});
            skArc(sketch, "E130.184", {"start": v(169.84, 10.24) * mm, "mid": v(169.46, 11.17) * mm, "end": v(168.53, 11.56) * mm});
            skPoint(sketch, "E130.185", {"position": v(169.84, -1.52) * mm});
            skArc(sketch, "E130.186", {"start": v(168.53, -1.52) * mm, "mid": v(169.46, -1.14) * mm, "end": v(169.84, -0.2) * mm});
            skPoint(sketch, "E130.187", {"position": v(143.6, 11.56) * mm});
            skArc(sketch, "E130.188", {"start": v(144.9, 11.56) * mm, "mid": v(143.98, 11.17) * mm, "end": v(143.6, 10.24) * mm});
            skPoint(sketch, "E130.189", {"position": v(143.6, -1.52) * mm});
            skArc(sketch, "E130.190", {"start": v(143.6, -0.2) * mm, "mid": v(143.98, -1.14) * mm, "end": v(144.9, -1.52) * mm});
            skLineSegment(sketch, "E130.191", {"start": v(-0.53, 19.68) * mm, "end": v(0.96, 19.68) * mm});
            skLineSegment(sketch, "E130.192", {"start": v(-0.33, 15.35) * mm, "end": v(0.96, 15.35) * mm});
            skLineSegment(sketch, "E130.193.0", {"start": v(-2.03, 15.35) * mm, "end": v(-0.33, 15.35) * mm});
            skLineSegment(sketch, "E130.193.1", {"start": v(-0.33, 15.35) * mm, "end": v(0.96, 15.35) * mm});
            skLineSegment(sketch, "E130.193.2", {"start": v(0.96, 15.35) * mm, "end": v(0.96, 19.68) * mm});
            skLineSegment(sketch, "E130.193.3", {"start": v(0.96, 19.68) * mm, "end": v(-0.53, 19.68) * mm});
            skLineSegment(sketch, "E130.193.4", {"start": v(-0.53, 19.68) * mm, "end": v(-2.03, 19.68) * mm});
            skLineSegment(sketch, "E130.193.5", {"start": v(-2.03, 19.68) * mm, "end": v(-2.03, 31.6) * mm});
            skLineSegment(sketch, "E130.193.6", {"start": v(-2.03, 31.6) * mm, "end": v(-12.94, 31.6) * mm});
            skLineSegment(sketch, "E130.193.7", {"start": v(-12.94, 31.6) * mm, "end": v(-12.94, 19.68) * mm});
            skLineSegment(sketch, "E130.193.8", {"start": v(-12.94, 19.68) * mm, "end": v(-30.43, 19.68) * mm});
            skArc(sketch, "E130.193.9", {"start": v(-30.43, 19.68) * mm, "mid": v(-31.35, 20.2) * mm, "end": v(-31.35, 21.25) * mm});
            skLineSegment(sketch, "E130.193.10", {"start": v(-31.35, 21.25) * mm, "end": v(-25.18, 31.6) * mm});
            skLineSegment(sketch, "E130.193.11", {"start": v(-25.18, 31.6) * mm, "end": v(-31.25, 31.6) * mm});
            skLineSegment(sketch, "E130.193.12", {"start": v(-31.25, 31.6) * mm, "end": v(-35.26, 31.6) * mm});
            skLineSegment(sketch, "E130.193.13", {"start": v(-35.26, 31.6) * mm, "end": v(-42.35, 19.59) * mm});
            skArc(sketch, "E130.193.14", {"start": v(-42.35, 19.59) * mm, "mid": v(-42.25, 16.75) * mm, "end": v(-39.77, 15.35) * mm});
            skLineSegment(sketch, "E130.193.15", {"start": v(-39.77, 15.35) * mm, "end": v(-12.94, 15.35) * mm});
            skLineSegment(sketch, "E130.193.16", {"start": v(-12.94, 15.35) * mm, "end": v(-12.94, 11.72) * mm});
            skLineSegment(sketch, "E130.193.17", {"start": v(-12.94, 11.72) * mm, "end": v(-2.03, 11.72) * mm});
            skLineSegment(sketch, "E130.193.18", {"start": v(-2.03, 11.72) * mm, "end": v(-2.03, 15.35) * mm});
            skLineSegment(sketch, "E131", {"start": v(0.96, 19.1) * mm, "end": v(4.7, 19.1) * mm});
            skLineSegment(sketch, "E132", {"start": v(0.96, 15.95) * mm, "end": v(4.7, 15.95) * mm});
            skLineSegment(sketch, "E133", {"start": v(3.28, 19.1) * mm, "end": v(0.96, 19.1) * mm});
            skLineSegment(sketch, "E134", {"start": v(-41.74, 16.12) * mm, "end": v(-52.01, 16.17) * mm});
            skLineSegment(sketch, "E135.trimOffspring", {"start": v(-62.04, 19.1) * mm, "end": v(-65.54, 19.1) * mm});
            skLineSegment(sketch, "E136.trimOffspring", {"start": v(-62.04, 16.2) * mm, "end": v(-65.54, 16.22) * mm});
            skLineSegment(sketch, "E137.trimOffspring", {"start": v(-42.55, 19.1) * mm, "end": v(-52.01, 19.1) * mm});
            skArc(sketch, "E138.0", {"start": v(87.35, 17.15) * mm, "mid": v(83.15, 15.61) * mm, "end": v(80.94, 11.72) * mm});
            skLineSegment(sketch, "E138.1", {"start": v(88.48, 17.15) * mm, "end": v(87.35, 17.15) * mm});
            skLineSegment(sketch, "E139", {"start": v(80.94, 11.72) * mm, "end": v(81.8, 11.72) * mm});
            skLineSegment(sketch, "E140", {"start": v(88.48, 17.15) * mm, "end": v(88.48, 16.3) * mm});
            skLineSegment(sketch, "E141", {"start": v(131.01, -0.39) * mm, "end": v(132.39, -0.39) * mm});
            skLineSegment(sketch, "E142", {"start": v(131.01, 3.72) * mm, "end": v(132.39, 3.72) * mm});
            skPoint(sketch, "E143", {"position": v(20.61, 19.1) * mm});
            skPoint(sketch, "E144", {"position": v(20.61, 15.95) * mm});
            skLineSegment(sketch, "E145", {"start": v(20.61, 19.1) * mm, "end": v(20.61, 15.95) * mm});
            skLineSegment(sketch, "E146", {"start": v(45.1, 19.1) * mm, "end": v(45.1, 16.28) * mm});
            skLineSegment(sketch, "E147", {"start": v(20.61, 19.1) * mm, "end": v(24.38, 19.1) * mm});
            skLineSegment(sketch, "E148", {"start": v(20.61, 15.95) * mm, "end": v(24.38, 15.95) * mm});
            skLineSegment(sketch, "E149", {"start": v(24.38, 19.1) * mm, "end": v(29.15, 20.81) * mm});
            skLineSegment(sketch, "E150", {"start": v(24.38, 15.95) * mm, "end": v(29.15, 14.23) * mm});
            skLineSegment(sketch, "E151", {"start": v(31.07, 20.81) * mm, "end": v(31.07, 14.23) * mm});
            skLineSegment(sketch, "E152", {"start": v(29.15, 20.81) * mm, "end": v(31.07, 20.81) * mm});
            skLineSegment(sketch, "E153", {"start": v(29.15, 14.23) * mm, "end": v(31.07, 14.23) * mm});
            skSolve(sketch);
        }
        {
            var Q0;
            Q0=qSketchRegion(id+"F0",true);
            extrude(context, id + "F2", {"entities" : qUnion([Q0]), "depth" : 4 * mm, "offsetDistance" : 25 * mm});
        }
        {
            var Q0;
            {var subQ2=sQuery(id+"F1.wireOp",EDGE,"E135.trimOffspring");Q0=makeQuery(id+"F1.imprint","IMPRINT",FACE,{"disambiguationData":[TD([[makeQuery(id+"F1.imprint","IMPRINT",EDGE,{"derivedFrom":subQ2}),1.0]])]});}
            var Q1;
            {var subQ0=sQuery(id+"F1.wireOp",EDGE,"E134");Q1=makeQuery(id+"F1.imprint","IMPRINT",FACE,{"disambiguationData":[TD([[makeQuery(id+"F1.imprint","IMPRINT",EDGE,{"derivedFrom":subQ0}),-1.0]])]});}
            var Q2;
            {var subQ5=sQuery(id+"F1.wireOp",EDGE,"E133");Q2=makeQuery(id+"F1.imprint","IMPRINT",FACE,{"disambiguationData":[TD([[makeQuery(id+"F1.imprint","IMPRINT",EDGE,{"derivedFrom":subQ5}),1.0]])]});}
            var Q3;
            Q3=makeQuery(id+"F1.imprint","IMPRINT",FACE,{"disambiguationData":[TD([[makeQuery(id+"F1.imprint","IMPRINT",EDGE,{"derivedFrom":sQuery(id+"F1.wireOp",EDGE,"E138.0")}),1.0]])]});
            var Q4;
            {var subQ4=sQuery(id+"F1.wireOp",EDGE,"E130.102");Q4=makeQuery(id+"F1.imprint","IMPRINT",FACE,{"disambiguationData":[TD([[makeQuery(id+"F1.imprint","IMPRINT",EDGE,{"derivedFrom":subQ4}),1.0]])]});}
            var Q5;
            Q5=makeQuery(id+"F1.imprint","IMPRINT",FACE,{"disambiguationData":[TD([[makeQuery(id+"F1.imprint","IMPRINT",EDGE,{"derivedFrom":sQuery(id+"F1.wireOp",EDGE,"E145")}),1.0]])]});
            extrude(context, id + "F3", {"entities" : qUnion([Q0, Q1, Q2, Q3, Q4, Q5]), "depth" : 1.5 * mm, "offsetDistance" : 25 * mm});
        }
        {
            var Q0;
            Q0=makeQuery(id+"F0.imprint","IMPRINT",FACE,{"disambiguationData":[TD([[makeQuery(id+"F0.imprint","IMPRINT",EDGE,{"derivedFrom":sQuery(id+"F0.wireOp",EDGE,"E95.bottom")}),-1.0]])]});
            var sketch = newSketch(context, id + "F4", { "sketchPlane" : qUnion([Q0])});
            skCircle(sketch, "E154", {"center": v(138.43, 10.41) * mm, "radius": 4 * mm});
            skCircle(sketch, "E155", {"center": v(124.85, -1.2) * mm, "radius": 4 * mm});
            skCircle(sketch, "E156", {"center": v(50.15, 26.53) * mm, "radius": 4 * mm});
            skCircle(sketch, "E157", {"center": v(-7.46, 17.6) * mm, "radius": 4 * mm});
            skCircle(sketch, "E158", {"center": v(-57.22, 22.35) * mm, "radius": 4 * mm});
            skCircle(sketch, "E159", {"center": v(-104.26, 25.15) * mm, "radius": 4 * mm});
            skCircle(sketch, "E160", {"center": v(177.08, 13.42) * mm, "radius": 2 * mm});
            skCircle(sketch, "E161", {"center": v(177.58, -2.9) * mm, "radius": 2 * mm});
            skCircle(sketch, "E162", {"center": v(87.83, -3.1) * mm, "radius": 2 * mm});
            skCircle(sketch, "E163", {"center": v(83.55, 20.28) * mm, "radius": 2 * mm});
            skCircle(sketch, "E164", {"center": v(-32.81, 27.25) * mm, "radius": 2 * mm});
            skCircle(sketch, "E165", {"center": v(-72.55, 14.76) * mm, "radius": 2 * mm});
            skSolve(sketch);
        }
        {
            var Q0;
            Q0=makeQuery(id+"F4.imprint","IMPRINT",FACE,{"disambiguationData":[TD([[makeQuery(id+"F4.imprint","IMPRINT",EDGE,{"derivedFrom":sQuery(id+"F4.wireOp",EDGE,"E160")}),1.0]])]});
            var Q1;
            Q1=makeQuery(id+"F4.imprint","IMPRINT",FACE,{"disambiguationData":[TD([[makeQuery(id+"F4.imprint","IMPRINT",EDGE,{"derivedFrom":sQuery(id+"F4.wireOp",EDGE,"E161")}),1.0]])]});
            var Q2;
            Q2=makeQuery(id+"F4.imprint","IMPRINT",FACE,{"disambiguationData":[TD([[makeQuery(id+"F4.imprint","IMPRINT",EDGE,{"derivedFrom":sQuery(id+"F4.wireOp",EDGE,"E162")}),1.0]])]});
            var Q3;
            Q3=makeQuery(id+"F4.imprint","IMPRINT",FACE,{"disambiguationData":[TD([[makeQuery(id+"F4.imprint","IMPRINT",EDGE,{"derivedFrom":sQuery(id+"F4.wireOp",EDGE,"E163")}),1.0]])]});
            var Q4;
            Q4=makeQuery(id+"F4.imprint","IMPRINT",FACE,{"disambiguationData":[TD([[makeQuery(id+"F4.imprint","IMPRINT",EDGE,{"derivedFrom":sQuery(id+"F4.wireOp",EDGE,"E164")}),1.0]])]});
            var Q5;
            Q5=makeQuery(id+"F4.imprint","IMPRINT",FACE,{"disambiguationData":[TD([[makeQuery(id+"F4.imprint","IMPRINT",EDGE,{"derivedFrom":sQuery(id+"F4.wireOp",EDGE,"E165")}),1.0]])]});
            var Q6;
            Q6=sQuery(id+"F4.wireOp",EDGE,"E160");
            var Q7;
            Q7=sQuery(id+"F4.wireOp",EDGE,"E161");
            var Q8;
            Q8=sQuery(id+"F4.wireOp",EDGE,"E162");
            var Q9;
            Q9=sQuery(id+"F4.wireOp",EDGE,"E163");
            var Q10;
            Q10=sQuery(id+"F4.wireOp",EDGE,"E164");
            var Q11;
            Q11=sQuery(id+"F4.wireOp",EDGE,"E165");
            extrude(context, id + "F5", {"entities" : qUnion([Q0, Q1, Q2, Q3, Q4, Q5]), "operationType" : NewBodyOperationType.REMOVE, "surfaceEntities" : qUnion([Q6, Q7, Q8, Q9, Q10, Q11]), "depth" : 1 * mm, "offsetDistance" : 25 * mm});
        }
        {
            var Q0;
            Q0=makeQuery(id+"F4.imprint","IMPRINT",FACE,{"disambiguationData":[TD([[makeQuery(id+"F4.imprint","IMPRINT",EDGE,{"derivedFrom":sQuery(id+"F4.wireOp",EDGE,"E154")}),1.0]])]});
            var Q1;
            Q1=makeQuery(id+"F4.imprint","IMPRINT",FACE,{"disambiguationData":[TD([[makeQuery(id+"F4.imprint","IMPRINT",EDGE,{"derivedFrom":sQuery(id+"F4.wireOp",EDGE,"E155")}),1.0]])]});
            var Q2;
            Q2=makeQuery(id+"F4.imprint","IMPRINT",FACE,{"disambiguationData":[TD([[makeQuery(id+"F4.imprint","IMPRINT",EDGE,{"derivedFrom":sQuery(id+"F4.wireOp",EDGE,"E156")}),1.0]])]});
            var Q3;
            Q3=makeQuery(id+"F4.imprint","IMPRINT",FACE,{"disambiguationData":[TD([[makeQuery(id+"F4.imprint","IMPRINT",EDGE,{"derivedFrom":sQuery(id+"F4.wireOp",EDGE,"E157")}),1.0]])]});
            var Q4;
            Q4=makeQuery(id+"F4.imprint","IMPRINT",FACE,{"disambiguationData":[TD([[makeQuery(id+"F4.imprint","IMPRINT",EDGE,{"derivedFrom":sQuery(id+"F4.wireOp",EDGE,"E158")}),1.0]])]});
            var Q5;
            Q5=makeQuery(id+"F4.imprint","IMPRINT",FACE,{"disambiguationData":[TD([[makeQuery(id+"F4.imprint","IMPRINT",EDGE,{"derivedFrom":sQuery(id+"F4.wireOp",EDGE,"E159")}),1.0]])]});
            extrude(context, id + "F6", {"entities" : qUnion([Q0, Q1, Q2, Q3, Q4, Q5]), "operationType" : NewBodyOperationType.REMOVE, "depth" : 2 * mm, "offsetDistance" : 25 * mm});
        }
        {
            var Q0;
            Q0=makeQuery(id+"F4.imprint","IMPRINT",FACE,{"disambiguationData":[TD([[makeQuery(id+"F4.imprint","IMPRINT",EDGE,{"derivedFrom":sQuery(id+"F4.wireOp",EDGE,"E156")}),1.0]])]});
            var Q1;
            Q1=makeQuery(id+"F4.imprint","IMPRINT",FACE,{"disambiguationData":[TD([[makeQuery(id+"F4.imprint","IMPRINT",EDGE,{"derivedFrom":sQuery(id+"F4.wireOp",EDGE,"E155")}),1.0]])]});
            var Q2;
            Q2=makeQuery(id+"F4.imprint","IMPRINT",FACE,{"disambiguationData":[TD([[makeQuery(id+"F4.imprint","IMPRINT",EDGE,{"derivedFrom":sQuery(id+"F4.wireOp",EDGE,"E154")}),1.0]])]});
            var Q3;
            Q3=sQuery(id+"F4.wireOp",EDGE,"E156");
            var Q4;
            Q4=sQuery(id+"F4.wireOp",EDGE,"E155");
            var Q5;
            Q5=sQuery(id+"F4.wireOp",EDGE,"E154");
            extrude(context, id + "F7", {"entities" : qUnion([Q0, Q1, Q2]), "operationType" : NewBodyOperationType.REMOVE, "surfaceEntities" : qUnion([Q3, Q4, Q5]), "depth" : 2 * mm, "offsetDistance" : 25 * mm});
        }
        {
            var Q0;
            Q0=makeQuery(id+"F4.imprint","IMPRINT",FACE,{"disambiguationData":[TD([[makeQuery(id+"F4.imprint","IMPRINT",EDGE,{"derivedFrom":sQuery(id+"F4.wireOp",EDGE,"E163")}),1.0]])]});
            var Q1;
            Q1=makeQuery(id+"F4.imprint","IMPRINT",FACE,{"disambiguationData":[TD([[makeQuery(id+"F4.imprint","IMPRINT",EDGE,{"derivedFrom":sQuery(id+"F4.wireOp",EDGE,"E162")}),1.0]])]});
            var Q2;
            Q2=makeQuery(id+"F4.imprint","IMPRINT",FACE,{"disambiguationData":[TD([[makeQuery(id+"F4.imprint","IMPRINT",EDGE,{"derivedFrom":sQuery(id+"F4.wireOp",EDGE,"E160")}),1.0]])]});
            var Q3;
            Q3=makeQuery(id+"F4.imprint","IMPRINT",FACE,{"disambiguationData":[TD([[makeQuery(id+"F4.imprint","IMPRINT",EDGE,{"derivedFrom":sQuery(id+"F4.wireOp",EDGE,"E161")}),1.0]])]});
            var Q4;
            Q4=sQuery(id+"F4.wireOp",EDGE,"E163");
            var Q5;
            Q5=sQuery(id+"F4.wireOp",EDGE,"E162");
            var Q6;
            Q6=sQuery(id+"F4.wireOp",EDGE,"E160");
            var Q7;
            Q7=sQuery(id+"F4.wireOp",EDGE,"E161");
            extrude(context, id + "F8", {"entities" : qUnion([Q0, Q1, Q2, Q3]), "operationType" : NewBodyOperationType.REMOVE, "surfaceEntities" : qUnion([Q4, Q5, Q6, Q7]), "depth" : 1 * mm, "offsetDistance" : 25 * mm});
        }
        {
            var Q0;
            Q0=makeQuery(id+"F2.opExtrude","CAP_FACE",FACE,{"disambiguationData":[OSD([sQuery(id+"F0.wireOp",EDGE,"E4.bottom"),sQuery(id+"F0.wireOp",EDGE,"E4.top"),sQuery(id+"F0.wireOp",EDGE,"E4.left"),sQuery(id+"F0.wireOp",EDGE,"E4.right"),sQuery(id+"F0.wireOp",EDGE,"E5.bottom"),sQuery(id+"F0.wireOp",EDGE,"E5.top"),sQuery(id+"F0.wireOp",EDGE,"E5.right"),sQuery(id+"F0.wireOp",EDGE,"E6.bottom"),sQuery(id+"F0.wireOp",EDGE,"E6.top"),sQuery(id+"F0.wireOp",EDGE,"E6.left"),sQuery(id+"F0.wireOp",EDGE,"E6.right"),sQuery(id+"F0.wireOp",EDGE,"E7.filletArc"),sQuery(id+"F0.wireOp",EDGE,"E8.filletArc"),sQuery(id+"F0.wireOp",EDGE,"E9.filletArc"),sQuery(id+"F0.wireOp",EDGE,"E10.filletArc"),sQuery(id+"F0.wireOp",EDGE,"E11.filletArc"),sQuery(id+"F0.wireOp",EDGE,"E12.filletArc"),sQuery(id+"F0.wireOp",EDGE,"E13.filletArc"),sQuery(id+"F0.wireOp",EDGE,"E14.trimOffspring"),sQuery(id+"F0.wireOp",EDGE,"E15.filletArc")])],"isStart":false});
            var Q1;
            Q1=makeQuery(id+"F2.opExtrude","CAP_FACE",FACE,{"disambiguationData":[OSD([sQuery(id+"F0.wireOp",EDGE,"E16"),sQuery(id+"F0.wireOp",EDGE,"E17"),sQuery(id+"F0.wireOp",EDGE,"E18.left"),sQuery(id+"F0.wireOp",EDGE,"E18.right")])],"isStart":false});
            var Q2;
            Q2=makeQuery(id+"F2.opExtrude","CAP_FACE",FACE,{"disambiguationData":[OSD([sQuery(id+"F0.wireOp",EDGE,"E19"),sQuery(id+"F0.wireOp",EDGE,"E20.left"),sQuery(id+"F0.wireOp",EDGE,"E20.right"),sQuery(id+"F0.wireOp",EDGE,"E21.bottom"),sQuery(id+"F0.wireOp",EDGE,"E21.top"),sQuery(id+"F0.wireOp",EDGE,"E21.left"),sQuery(id+"F0.wireOp",EDGE,"E22"),sQuery(id+"F0.wireOp",EDGE,"E23"),sQuery(id+"F0.wireOp",EDGE,"E25.trimOffspring"),sQuery(id+"F0.wireOp",EDGE,"E26.trimOffspring"),sQuery(id+"F0.wireOp",EDGE,"E27.trimOffspring"),sQuery(id+"F0.wireOp",EDGE,"E28.trimOffspring"),sQuery(id+"F0.wireOp",EDGE,"E20.top"),sQuery(id+"F0.wireOp",EDGE,"E20.bottom"),sQuery(id+"F0.wireOp",EDGE,"E29.trimOffspring"),sQuery(id+"F0.wireOp",EDGE,"E30"),sQuery(id+"F0.wireOp",EDGE,"E31"),sQuery(id+"F0.wireOp",EDGE,"E118"),sQuery(id+"F0.wireOp",EDGE,"E119")])],"isStart":false});
            var Q3;
            Q3=makeQuery(id+"F2.opExtrude","CAP_FACE",FACE,{"disambiguationData":[OSD([sQuery(id+"F0.wireOp",EDGE,"E32"),sQuery(id+"F0.wireOp",EDGE,"E33"),sQuery(id+"F0.wireOp",EDGE,"E35"),sQuery(id+"F0.wireOp",EDGE,"E36"),sQuery(id+"F0.wireOp",EDGE,"E37"),sQuery(id+"F0.wireOp",EDGE,"E38.bottom"),sQuery(id+"F0.wireOp",EDGE,"E38.top"),sQuery(id+"F0.wireOp",EDGE,"E38.right"),sQuery(id+"F0.wireOp",EDGE,"E39.bottom"),sQuery(id+"F0.wireOp",EDGE,"E39.top"),sQuery(id+"F0.wireOp",EDGE,"E39.left"),sQuery(id+"F0.wireOp",EDGE,"E39.right"),sQuery(id+"F0.wireOp",EDGE,"E40.trimOffspring"),sQuery(id+"F0.wireOp",EDGE,"E41.filletArc"),sQuery(id+"F0.wireOp",EDGE,"E42.filletArc"),sQuery(id+"F0.wireOp",EDGE,"E43.filletArc"),sQuery(id+"F0.wireOp",EDGE,"E44.filletArc"),sQuery(id+"F0.wireOp",EDGE,"E45.filletArc"),sQuery(id+"F0.wireOp",EDGE,"E46.filletArc"),sQuery(id+"F0.wireOp",EDGE,"E47.filletArc"),sQuery(id+"F0.wireOp",EDGE,"E48.filletArc"),sQuery(id+"F0.wireOp",EDGE,"E49.filletArc"),sQuery(id+"F0.wireOp",EDGE,"E122.0"),sQuery(id+"F0.wireOp",EDGE,"E122.1"),sQuery(id+"F0.wireOp",EDGE,"E123")])],"isStart":false});
            var Q4;
            Q4=makeQuery(id+"F2.opExtrude","CAP_FACE",FACE,{"disambiguationData":[OSD([sQuery(id+"F0.wireOp",EDGE,"E50"),sQuery(id+"F0.wireOp",EDGE,"E51"),sQuery(id+"F0.wireOp",EDGE,"E52"),sQuery(id+"F0.wireOp",EDGE,"E53"),sQuery(id+"F0.wireOp",EDGE,"E54"),sQuery(id+"F0.wireOp",EDGE,"E55"),sQuery(id+"F0.wireOp",EDGE,"E56"),sQuery(id+"F0.wireOp",EDGE,"E57"),sQuery(id+"F0.wireOp",EDGE,"E58"),sQuery(id+"F0.wireOp",EDGE,"E59"),sQuery(id+"F0.wireOp",EDGE,"E60"),sQuery(id+"F0.wireOp",EDGE,"E61"),sQuery(id+"F0.wireOp",EDGE,"E62"),sQuery(id+"F0.wireOp",EDGE,"E63"),sQuery(id+"F0.wireOp",EDGE,"E64"),sQuery(id+"F0.wireOp",EDGE,"E65"),sQuery(id+"F0.wireOp",EDGE,"E66"),sQuery(id+"F0.wireOp",EDGE,"E67"),sQuery(id+"F0.wireOp",EDGE,"E68"),sQuery(id+"F0.wireOp",EDGE,"E69"),sQuery(id+"F0.wireOp",EDGE,"E70.trimOffspring"),sQuery(id+"F0.wireOp",EDGE,"E71.trimOffspring"),sQuery(id+"F0.wireOp",EDGE,"E74"),sQuery(id+"F0.wireOp",EDGE,"E75.filletArc"),sQuery(id+"F0.wireOp",EDGE,"E76.filletArc"),sQuery(id+"F0.wireOp",EDGE,"E77.filletArc"),sQuery(id+"F0.wireOp",EDGE,"E78.filletArc"),sQuery(id+"F0.wireOp",EDGE,"E79.filletArc"),sQuery(id+"F0.wireOp",EDGE,"E80.filletArc"),sQuery(id+"F0.wireOp",EDGE,"E81.filletArc"),sQuery(id+"F0.wireOp",EDGE,"E82.filletArc"),sQuery(id+"F0.wireOp",EDGE,"E83"),sQuery(id+"F0.wireOp",EDGE,"E84.filletArc"),sQuery(id+"F0.wireOp",EDGE,"E85.filletArc"),sQuery(id+"F0.wireOp",EDGE,"E86"),sQuery(id+"F0.wireOp",EDGE,"E87.filletArc"),sQuery(id+"F0.wireOp",EDGE,"E88.filletArc"),sQuery(id+"F0.wireOp",EDGE,"E89.filletArc"),sQuery(id+"F0.wireOp",EDGE,"E90.filletArc")])],"isStart":false});
            var Q5;
            Q5=makeQuery(id+"F2.opExtrude","CAP_FACE",FACE,{"disambiguationData":[OSD([sQuery(id+"F0.wireOp",EDGE,"E95.bottom"),sQuery(id+"F0.wireOp",EDGE,"E95.top"),sQuery(id+"F0.wireOp",EDGE,"E95.left"),sQuery(id+"F0.wireOp",EDGE,"E95.right"),sQuery(id+"F0.wireOp",EDGE,"E96"),sQuery(id+"F0.wireOp",EDGE,"E97"),sQuery(id+"F0.wireOp",EDGE,"E98"),sQuery(id+"F0.wireOp",EDGE,"E99"),sQuery(id+"F0.wireOp",EDGE,"E100"),sQuery(id+"F0.wireOp",EDGE,"E101"),sQuery(id+"F0.wireOp",EDGE,"E102"),sQuery(id+"F0.wireOp",EDGE,"E103.trimOffspring"),sQuery(id+"F0.wireOp",EDGE,"E104.filletArc"),sQuery(id+"F0.wireOp",EDGE,"E105.filletArc"),sQuery(id+"F0.wireOp",EDGE,"E106.filletArc"),sQuery(id+"F0.wireOp",EDGE,"E107.filletArc"),sQuery(id+"F0.wireOp",EDGE,"E108.filletArc"),sQuery(id+"F0.wireOp",EDGE,"E109.filletArc"),sQuery(id+"F0.wireOp",EDGE,"E110"),sQuery(id+"F0.wireOp",EDGE,"E111"),sQuery(id+"F0.wireOp",EDGE,"E112"),sQuery(id+"F0.wireOp",EDGE,"E113"),sQuery(id+"F0.wireOp",EDGE,"E114.filletArc"),sQuery(id+"F0.wireOp",EDGE,"E115.filletArc"),sQuery(id+"F0.wireOp",EDGE,"E116.filletArc"),sQuery(id+"F0.wireOp",EDGE,"E117.filletArc")])],"isStart":false});
            var Q6;
            Q6=makeQuery(id+"F2.opExtrude","CAP_FACE",FACE,{"disambiguationData":[OSD([sQuery(id+"F0.wireOp",EDGE,"E34.bottom"),sQuery(id+"F0.wireOp",EDGE,"E34.top"),sQuery(id+"F0.wireOp",EDGE,"E34.left"),sQuery(id+"F0.wireOp",EDGE,"E34.right")])],"isStart":false});
            fillet(context, id + "F9", {"entities" : qUnion([Q0, Q1, Q2, Q3, Q4, Q5, Q6]), "radius" : 1 * mm, "tangentPropagation" : true, "allowEdgeOverflow" : false});
        }
        {
            var Q0;
            {var subQ0=sQuery(id+"F0.wireOp",EDGE,"E125");Q0=makeQuery(id+"F0.imprint","IMPRINT",FACE,{"disambiguationData":[TD([[makeQuery(id+"F0.imprint","IMPRINT",EDGE,{"derivedFrom":subQ0}),-1.0]])]});}
            extrude(context, id + "F10", {"entities" : qUnion([Q0]), "operationType" : NewBodyOperationType.REMOVE, "depth" : 1.5 * mm, "offsetDistance" : 25 * mm});
        }
    });
